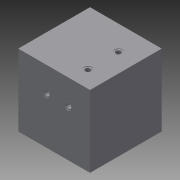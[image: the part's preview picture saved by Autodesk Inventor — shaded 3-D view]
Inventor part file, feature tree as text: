
AUTODESK INVENTOR PART (.ipt)
format: ipt  version: 2014 (Build 180170000, 170)  size: 273,920 bytes
history: native  units: mm
features: other x48, sketch x7, extrude x1
ambient origin geometry x8: Origin, YZ Plane, XZ Plane, XY Plane, X Axis, Y Axis, Z Axis, Center Point
bodies: Body1 (feature_tree)
feature tree (56):
  extrude  "拉伸1"  TaperAngle=0.0deg  [1 undecoded]
  other  "UCS1"
  other  "UCS2"
  other  "UCS3"
  other  "UCS4"
  other  "UCS5"
  other  "UCS6"
  sketch  "草图1"  dims[d0=300.0mm d1=0.0mm]
  other  "UCS1: YZ 平面"
  other  "UCS1: XZ 平面"
  other  "UCS1: XY 平面"
  other  "UCS1: X 轴"
  other  "UCS1: Y 轴"
  other  "UCS1: Z 轴"
  other  "UCS1: 原点"
  other  "UCS2: YZ 平面"
  other  "UCS2: XZ 平面"
  other  "UCS2: XY 平面"
  other  "UCS2: X 轴"
  other  "UCS2: Y 轴"
  other  "UCS2: Z 轴"
  other  "UCS2: 原点"
  other  "UCS3: YZ 平面"
  other  "UCS3: XZ 平面"
  other  "UCS3: XY 平面"
  other  "UCS3: X 轴"
  other  "UCS3: Y 轴"
  other  "UCS3: Z 轴"
  other  "UCS3: 原点"
  other  "UCS4: YZ 平面"
  other  "UCS4: XZ 平面"
  other  "UCS4: XY 平面"
  other  "UCS4: X 轴"
  other  "UCS4: Y 轴"
  other  "UCS4: Z 轴"
  other  "UCS4: 原点"
  other  "UCS5: YZ 平面"
  other  "UCS5: XZ 平面"
  other  "UCS5: XY 平面"
  other  "UCS5: X 轴"
  other  "UCS5: Y 轴"
  other  "UCS5: Z 轴"
  other  "UCS5: 原点"
  other  "UCS6: YZ 平面"
  other  "UCS6: XZ 平面"
  other  "UCS6: XY 平面"
  other  "UCS6: X 轴"
  other  "UCS6: Y 轴"
  other  "UCS6: Z 轴"
  other  "UCS6: 原点"
  sketch  "草图2"  dims[d2=0.0mm d3=0.0mm d4=0.0mm d5=0.0mm d6=0.0mm d7=0.0mm]
  sketch  "草图3"  dims[d8=0.0mm d9=0.0mm d10=0.0mm d11=0.0mm d12=0.0mm d13=0.0mm]
  sketch  "草图4"  dims[d14=0.0mm d15=0.0mm d16=0.0mm d17=0.0mm d18=0.0mm d19=0.0mm]
  sketch  "草图6"  dims[d20=0.0mm d21=0.0mm d22=0.0mm d23=0.0mm d24=0.0mm d25=0.0mm]
  sketch  "草图7"  dims[d26=0.0mm d27=0.0mm d28=0.0mm d29=0.0mm d30=0.0mm d31=0.0mm]
  sketch  "草图8"  dims[d32=0.0mm d33=0.0mm d34=0.0mm d35=0.0mm d36=0.0mm d37=0.0mm d38=0.0mm d42=0.0mm d46=0.0mm d53=0.0mm d57=0.0mm d61=0.0mm]
note: 1 required parameter value undecoded (feature->parameter linkage not recoverable at this tier; creation-order binding heuristic only, values carry confidence <= 0.55)
